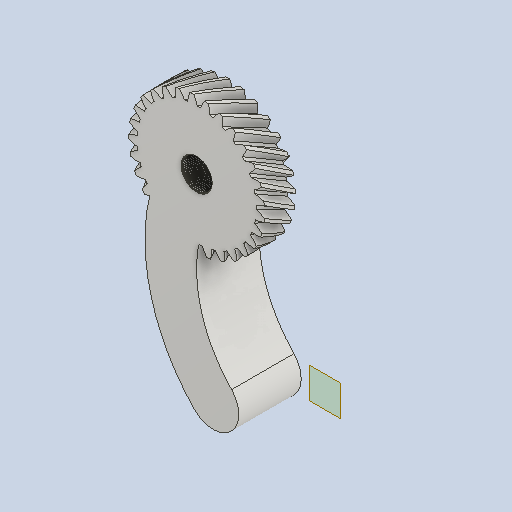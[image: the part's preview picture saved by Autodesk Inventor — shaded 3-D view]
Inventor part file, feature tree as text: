
AUTODESK INVENTOR PART (.ipt)
format: ipt  version: 2024 (Build 280153000, 153)  size: 1,945,600 bytes
history: native  units: mm (DEFAULTED — no unit token found)
features: reference x193, other x8, extrude x4, plane x4, sketch x4, projected_geometry x1
ambient origin geometry x8: Origin, YZ Plane, XZ Plane, XY Plane, X Axis, Y Axis, Z Axis, Center Point
bodies: Solid1 (feature_tree)
feature tree (214):
  extrude  "Extrusion1"  Depth=5.0mm TaperAngle=0.0deg
  plane  "Work Plane2"
  plane  "Work Plane8"
  plane  "Work Plane9"
  other  "Spur Gear"
  extrude  "Extrusion2"  Depth=10.0mm TaperAngle=0.0deg
  plane  "Work Plane11"
  extrude  "Extrusion3"  Depth=20.0mm TaperAngle=0.0deg
  extrude  "Extrusion4"  TaperAngle=0.0deg  [1 undecoded]
  sketch  "Sketch1"  dims[d0=21.801031mm d1=5.0mm d2=0.0mm]
  other  "Srf1"
  sketch  "Sketch3"  dims[d3=20.091789mm d4=10.0mm d5=0.0mm]
  sketch  "Sketch4"  dims[d16=20.0mm d17=0.0mm d34=1.083308mm]
  reference  "Reference1"
  reference  "Reference2"
  reference  "Reference3"
  reference  "Reference4"
  reference  "Reference5"
  reference  "Reference6"
  reference  "Reference7"
  reference  "Reference8"
  reference  "Reference9"
  reference  "Reference10"
  reference  "Reference11"
  reference  "Reference12"
  reference  "Reference13"
  reference  "Reference14"
  reference  "Reference15"
  reference  "Reference16"
  reference  "Reference17"
  reference  "Reference18"
  reference  "Reference19"
  reference  "Reference20"
  reference  "Reference21"
  reference  "Reference22"
  reference  "Reference23"
  reference  "Reference24"
  reference  "Reference25"
  reference  "Reference26"
  reference  "Reference27"
  reference  "Reference28"
  reference  "Reference29"
  reference  "Reference30"
  reference  "Reference31"
  reference  "Reference32"
  reference  "Reference33"
  reference  "Reference34"
  reference  "Reference35"
  reference  "Reference36"
  reference  "Reference37"
  reference  "Reference38"
  reference  "Reference39"
  reference  "Reference40"
  reference  "Reference41"
  reference  "Reference42"
  reference  "Reference43"
  reference  "Reference44"
  reference  "Reference45"
  reference  "Reference46"
  reference  "Reference47"
  reference  "Reference48"
  reference  "Reference49"
  reference  "Reference50"
  reference  "Reference51"
  reference  "Reference52"
  reference  "Reference53"
  reference  "Reference54"
  reference  "Reference55"
  reference  "Reference56"
  reference  "Reference57"
  reference  "Reference58"
  reference  "Reference59"
  reference  "Reference60"
  reference  "Reference61"
  reference  "Reference62"
  reference  "Reference63"
  reference  "Reference64"
  reference  "Reference65"
  reference  "Reference66"
  reference  "Reference67"
  reference  "Reference68"
  reference  "Reference69"
  reference  "Reference70"
  reference  "Reference71"
  reference  "Reference72"
  reference  "Reference73"
  reference  "Reference74"
  reference  "Reference75"
  reference  "Reference76"
  reference  "Reference77"
  reference  "Reference78"
  reference  "Reference79"
  reference  "Reference80"
  reference  "Reference81"
  reference  "Reference82"
  reference  "Reference83"
  reference  "Reference84"
  reference  "Reference85"
  reference  "Reference86"
  reference  "Reference87"
  reference  "Reference88"
  reference  "Reference89"
  reference  "Reference90"
  reference  "Reference91"
  reference  "Reference92"
  reference  "Reference93"
  reference  "Reference94"
  reference  "Reference95"
  reference  "Reference96"
  reference  "Reference97"
  reference  "Reference98"
  reference  "Reference99"
  reference  "Reference100"
  reference  "Reference101"
  reference  "Reference102"
  reference  "Reference103"
  reference  "Reference104"
  reference  "Reference105"
  reference  "Reference106"
  reference  "Reference107"
  reference  "Reference108"
  reference  "Reference109"
  reference  "Reference110"
  reference  "Reference111"
  reference  "Reference112"
  reference  "Reference113"
  reference  "Reference114"
  reference  "Reference115"
  reference  "Reference116"
  reference  "Reference117"
  reference  "Reference118"
  reference  "Reference119"
  reference  "Reference120"
  reference  "Reference121"
  reference  "Reference122"
  reference  "Reference123"
  reference  "Reference124"
  reference  "Reference125"
  reference  "Reference126"
  reference  "Reference127"
  reference  "Reference128"
  reference  "Reference129"
  reference  "Reference130"
  reference  "Reference131"
  reference  "Reference132"
  reference  "Reference133"
  reference  "Reference134"
  reference  "Reference135"
  reference  "Reference136"
  reference  "Reference137"
  reference  "Reference138"
  reference  "Reference139"
  reference  "Reference140"
  reference  "Reference141"
  reference  "Reference142"
  reference  "Reference143"
  reference  "Reference144"
  reference  "Reference145"
  reference  "Reference146"
  reference  "Reference147"
  reference  "Reference148"
  reference  "Reference149"
  reference  "Reference150"
  reference  "Reference151"
  reference  "Reference152"
  reference  "Reference153"
  reference  "Reference154"
  reference  "Reference155"
  reference  "Reference156"
  reference  "Reference157"
  reference  "Reference158"
  reference  "Reference159"
  reference  "Reference160"
  reference  "Reference161"
  reference  "Reference162"
  reference  "Reference163"
  reference  "Reference164"
  reference  "Reference165"
  reference  "Reference166"
  reference  "Reference167"
  reference  "Reference168"
  reference  "Reference169"
  reference  "Reference170"
  reference  "Reference171"
  reference  "Reference172"
  reference  "Reference173"
  reference  "Reference174"
  reference  "Reference175"
  reference  "Reference176"
  reference  "Reference177"
  reference  "Reference178"
  reference  "Reference179"
  reference  "Reference180"
  reference  "Reference181"
  reference  "Reference182"
  reference  "Reference183"
  reference  "Reference184"
  reference  "Reference185"
  reference  "Reference186"
  reference  "Reference187"
  reference  "Reference188"
  reference  "Reference189"
  reference  "Reference190"
  reference  "Reference191"
  reference  "Reference192"
  reference  "Reference193"
  sketch  "Sketch5"  dims[d39=0.0mm d41=0.0mm d43=20.0mm d46=20.0mm d47=0.0mm d48=0.0mm d49=5.0mm d50=10.0mm d51=0.0mm d52=2.0mm d53=3.0mm d54=0.0mm d55=0.0mm d56=40.0mm d57=5.0mm d58=5.0mm d59=20.0mm d60=56.568542mm d61=30.0mm d62=10.0mm d63=0.0mm]
  projected_geometry  "Projected Loop1"
  other  "Pitch Diameter"
  other  "<userpath> windows\Documents\Inventor\Robotska_roka\Assembly4.iam"
  other  "Assembly4.iam"
  other  "SG90 - Micro Servo 9g - Tower Pro:3"
  other  "Tower Pro - Micro Servo 9g - SG90.1_12"
  other  "Tower Pro - Micro Servo 9g - SG90.1_11"
note: 1 required parameter value undecoded (feature->parameter linkage not recoverable at this tier; creation-order binding heuristic only, values carry confidence <= 0.55)
